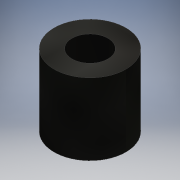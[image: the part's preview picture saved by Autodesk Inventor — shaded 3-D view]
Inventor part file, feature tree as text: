
AUTODESK INVENTOR PART (.ipt)
format: ipt  version: 2016 (Build 200138000, 138)  size: 94,720 bytes
history: native  units: mm
features: other x1, extrude x1, sketch x1
ambient origin geometry x8: Origin, YZ Plane, XZ Plane, XY Plane, X Axis, Y Axis, Z Axis, Center Point
bodies: Body1 (feature_tree)
feature tree (3):
  other  "ソリッド1"
  extrude  "押し出し1"  Depth=6.0mm
  sketch  "スケッチ1"
